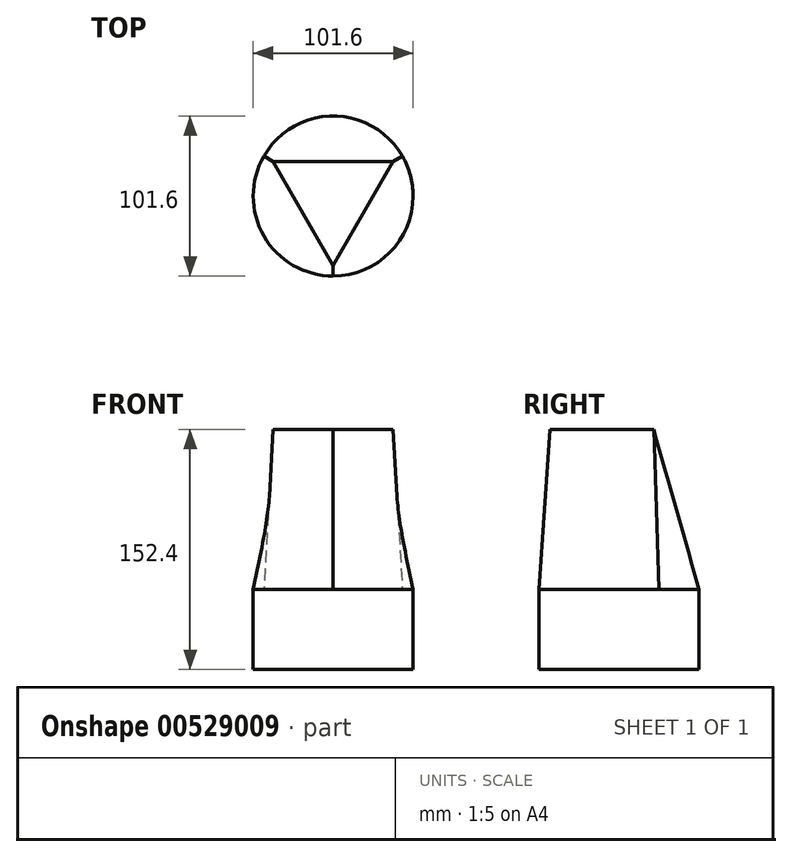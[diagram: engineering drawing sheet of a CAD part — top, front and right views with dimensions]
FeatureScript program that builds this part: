
annotation { "Feature Type Name" : "Feature", "Feature Type Description" : "" }
export const myFeature = defineFeature(function(context is Context, id is Id, definition is map)
    precondition{}
    {
        {
            var Q0;
            Q0=qCreatedBy(makeId("Front.planeOp"),FACE);
            var sketch = newSketch(context, id + "F0", { "sketchPlane" : qUnion([Q0])});
            skLineSegment(sketch, "E0.bottom", {"start": v(-25.4, 25.4) * mm, "end": v(25.4, 25.4) * mm});
            skLineSegment(sketch, "E0.top", {"start": v(-25.4, -25.4) * mm, "end": v(25.4, -25.4) * mm});
            skLineSegment(sketch, "E0.left", {"start": v(-25.4, 25.4) * mm, "end": v(-25.4, -25.4) * mm});
            skLineSegment(sketch, "E0.right", {"start": v(25.4, 25.4) * mm, "end": v(25.4, -25.4) * mm});
            skSolve(sketch);
        }
        {
            var Q0;
            Q0=makeQuery(id+"F0.imprint","IMPRINT",FACE,{"disambiguationData":[TD([[makeQuery(id+"F0.imprint","IMPRINT",EDGE,{"derivedFrom":sQuery(id+"F0.wireOp",EDGE,"E0.bottom")}),-1.0]])]});
            var Q1;
            Q1=sQuery(id+"F0.wireOp",EDGE,"E0.right");
            revolve(context, id + "F1", {"entities" : qUnion([Q0]), "axis" : qUnion([Q1]), "revolveType" : RevolveType.FULL});
        }
        {
            var Q0;
            Q0=makeQuery(id+"F1.opRevolve","SWEPT_FACE",FACE,{"disambiguationData":[OSD([sQuery(id+"F0.wireOp",EDGE,"E0.bottom")])]});
            cPlane(context, id + "F2", {"entities" : qUnion([Q0]), "cplaneType" : CPlaneType.OFFSET, "offset" : 101.6 * mm, "width" : 152.4 * mm, "height" : 152.4 * mm});
        }
        {
            var Q0;
            Q0=qCreatedBy(id+"F2.planeOp",FACE);
            var sketch = newSketch(context, id + "F3", { "sketchPlane" : qUnion([Q0])});
            skCircle(sketch, "E1.cCircle", {"center": v(25.4, 0) * mm, "radius": 22 * mm, "construction": true});
            skLineSegment(sketch, "E1.0", {"start": v(-12.7, 22) * mm, "end": v(63.5, 22) * mm});
            skLineSegment(sketch, "E1.1", {"start": v(63.5, 22) * mm, "end": v(25.4, -44) * mm});
            skLineSegment(sketch, "E1.2", {"start": v(25.4, -44) * mm, "end": v(-12.7, 22) * mm});
            skPoint(sketch, "E1.0.midPoint", {"position": v(25.4, 22) * mm});
            skSolve(sketch);
        }
        {
            var Q0;
            Q0=makeQuery(id+"F1.opRevolve","SWEPT_FACE",FACE,{"disambiguationData":[OSD([sQuery(id+"F0.wireOp",EDGE,"E0.bottom")])]});
            var sketch = newSketch(context, id + "F4", { "sketchPlane" : qUnion([Q0])});
            skCircle(sketch, "E2", {"center": v(25.4, 0) * mm, "radius": 50.8 * mm});
            skSolve(sketch);
        }
        {
            var Q1;
            Q1 = qSketchRegion(id + "F3", true);
            var Q2;
            Q2 = qSketchRegion(id + "F4", true);
            loft(context, id + "F5", {"operationType" : NewBodyOperationType.ADD, "sheetProfilesArray" : [{ "sheetProfileEntities" : qUnion([Q1]) }, { "sheetProfileEntities" : qUnion([Q2]) }]});
        }
    });
